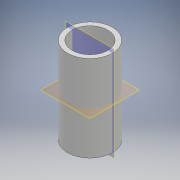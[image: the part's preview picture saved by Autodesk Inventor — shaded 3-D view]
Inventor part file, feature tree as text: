
AUTODESK INVENTOR PART (.ipt)
format: ipt  version: 2017 (Build 210142000, 142)  size: 97,280 bytes
history: native  units: mm
features: extrude x1, sketch x1
ambient origin geometry x8: Origin, YZ Plane, XZ Plane, XY Plane, X Axis, Y Axis, Z Axis, Center Point
bodies: Solid1 (feature_tree)
feature tree (2):
  extrude  "Extrusion1"  Depth=50.0mm
  sketch  "Sketch1"  dims[d0=26.0mm d1=2.7mm d2=50.0mm d3=0.0mm]
